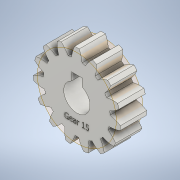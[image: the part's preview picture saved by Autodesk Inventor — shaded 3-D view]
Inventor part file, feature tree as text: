
AUTODESK INVENTOR PART (.ipt)
format: ipt  version: 2021 (Build 250183000, 183)  size: 439,296 bytes
history: native  units: mm (DEFAULTED — no unit token found)
features: sketch x4, plane x3, other x3, extrude x2, emboss x1
ambient origin geometry x8: Origin, YZ Plane, XZ Plane, XY Plane, X Axis, Y Axis, Z Axis, Center Point
bodies: Solid1 (feature_tree)
feature tree (13):
  extrude  "Extrusion1"  Depth=5.0mm TaperAngle=0.0deg
  plane  "Work Plane2"
  plane  "Work Plane8"
  plane  "Work Plane9"
  other  "Spur Gear"
  extrude  "Extrusion2"  Depth=10.0mm TaperAngle=0.0deg
  emboss  "Emboss1"
  sketch  "Sketch1"  dims[d0=16.6mm d1=5.0mm d2=0.0mm]
  sketch  "Sketch2"  dims[d3=15.0mm d4=10.0mm d5=0.0mm]
  other  "Srf1"
  sketch  "Sketch4"  dims[d16=22.5mm]
  sketch  "Sketch5"  dims[d17=0.0mm d34=2.094395mm d39=0.0mm d41=0.0mm d43=22.5mm d46=22.5mm d47=0.0mm d48=0.0mm d57=5.0mm d58=2.0mm d59=1.5mm d60=5.0mm d61=0.0mm d62=1.0mm d63=0.0mm]
  other  "Pitch Diameter"
